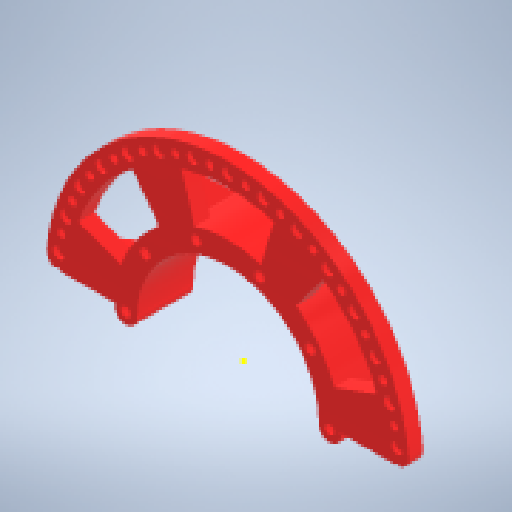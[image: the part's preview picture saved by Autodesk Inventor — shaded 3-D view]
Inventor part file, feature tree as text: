
AUTODESK INVENTOR PART (.ipt)
format: ipt  version: 2024 (Build 280153000, 153)  size: 387,072 bytes
history: native  units: mm
features: sketch x8, extrude x3, hole x3, pattern_circular x3, projected_geometry x3, fillet x2, other x1, revolve x1
ambient origin geometry x8: Origin, YZ Plane, XZ Plane, XY Plane, X Axis, Y Axis, Z Axis, Center Point
bodies: Body1 (feature_tree)
feature tree (24):
  other  "ソリッド1"
  extrude  "押し出し1"  Depth=160.0mm
  hole  "穴1"  [1 undecoded]
  pattern_circular  "円形状パターン1"  Count=8  [1 undecoded]
  extrude  "押し出し2"  Depth=100.0mm
  extrude  "押し出し3"  Depth=1.0mm
  revolve  "回転1"
  hole  "穴2"  [1 undecoded]
  pattern_circular  "円形状パターン2"  [2 undecoded]
  fillet  "フィレット1"  Radius=5.759587mm
  fillet  "フィレット2"  Radius=7.0mm
  hole  "穴3"  [1 undecoded]
  pattern_circular  "円形状パターン3"  [2 undecoded]
  sketch  "スケッチ8"
  sketch  "スケッチ1"
  sketch  "スケッチ2"
  sketch  "スケッチ3"
  projected_geometry  "投影ループ1"
  sketch  "スケッチ4"
  projected_geometry  "投影ループ2"
  sketch  "スケッチ5"
  projected_geometry  "投影ループ3"
  sketch  "スケッチ6"
  sketch  "スケッチ7"
note: 8 required parameter values undecoded (feature->parameter linkage not recoverable at this tier; creation-order binding heuristic only, values carry confidence <= 0.55)
